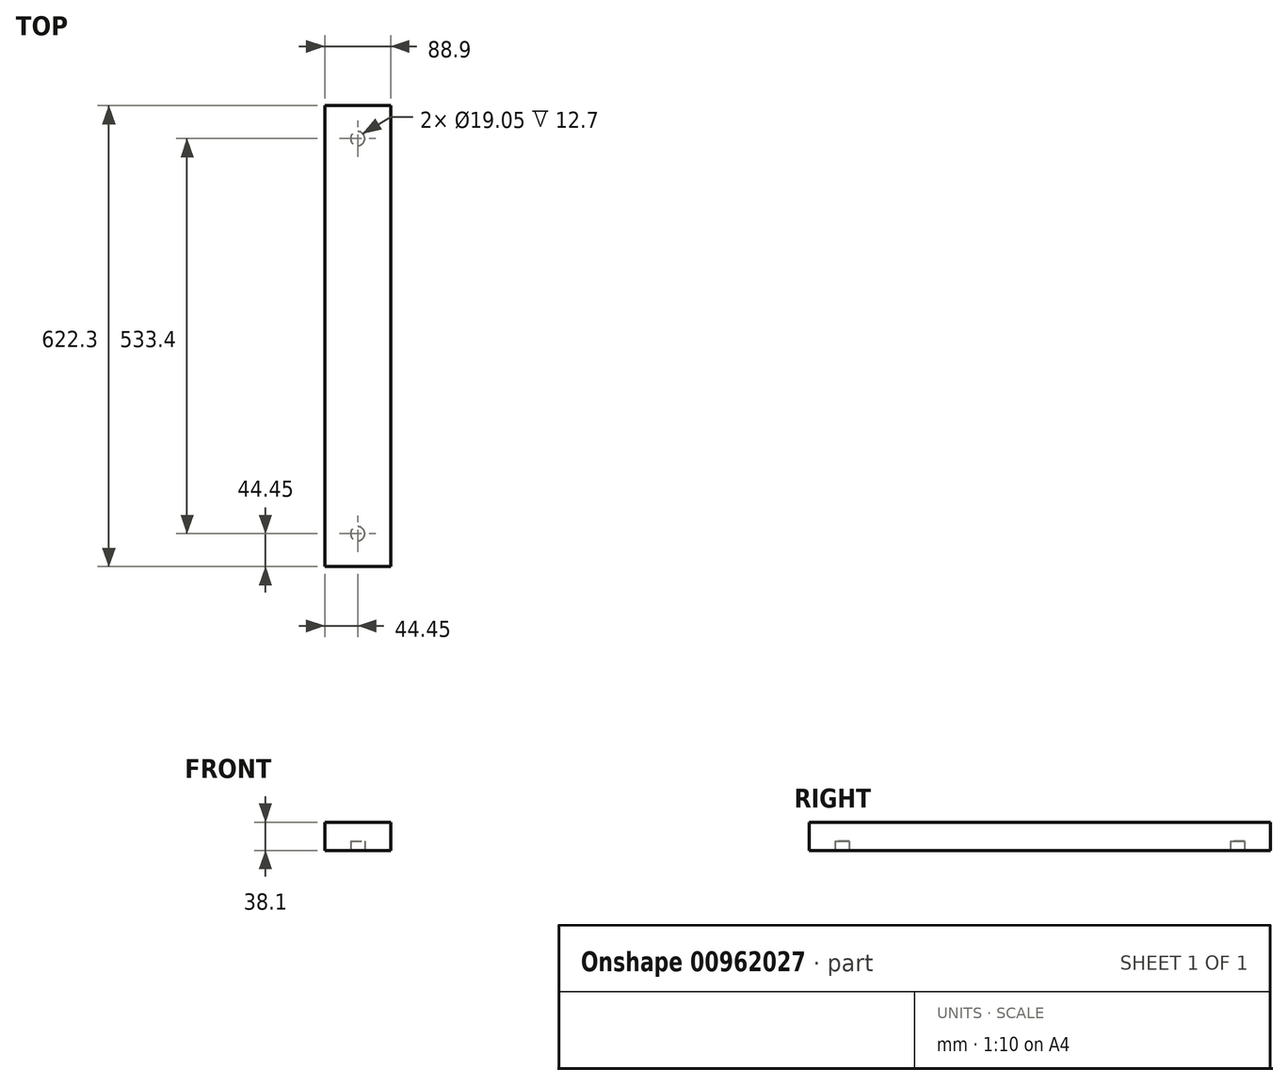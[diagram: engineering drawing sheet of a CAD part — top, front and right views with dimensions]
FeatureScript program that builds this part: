
annotation { "Feature Type Name" : "Feature", "Feature Type Description" : "" }
export const myFeature = defineFeature(function(context is Context, id is Id, definition is map)
    precondition{}
    {
        {
            var Q0;
            Q0=qCreatedBy(makeId("Front.planeOp"),FACE);
            var sketch = newSketch(context, id + "F0", { "sketchPlane" : qUnion([Q0])});
            skLineSegment(sketch, "E0.bottom", {"start": v(44.45, 19.05) * mm, "end": v(-44.45, 19.05) * mm});
            skLineSegment(sketch, "E0.top", {"start": v(44.45, -19.05) * mm, "end": v(-44.45, -19.05) * mm});
            skLineSegment(sketch, "E0.left", {"start": v(44.45, 19.05) * mm, "end": v(44.45, -19.05) * mm});
            skLineSegment(sketch, "E0.right", {"start": v(-44.45, 19.05) * mm, "end": v(-44.45, -19.05) * mm});
            skPoint(sketch, "E0.middle", {"position": v(0, 0) * mm});
            skSolve(sketch);
        }
        {
            var Q0;
            Q0 = qSketchRegion(id + "F0", true);
            extrude(context, id + "F1", {"entities" : qUnion([Q0]), "endBound" : BoundingType.SYMMETRIC, "depth" : 622.3 * mm, "offsetDistance" : 25.4 * mm});
        }
        {
            var Q0;
            Q0=makeQuery(id+"F1.opExtrude","SWEPT_FACE",FACE,{"disambiguationData":[OSD([sQuery(id+"F0.wireOp",EDGE,"E0.top")])]});
            var sketch = newSketch(context, id + "F2", { "sketchPlane" : qUnion([Q0])});
            skCircle(sketch, "E1", {"center": v(0, 266.7) * mm, "radius": 9.53 * mm});
            skCircle(sketch, "E2", {"center": v(0, -266.7) * mm, "radius": 9.53 * mm});
            skSolve(sketch);
        }
        {
            var Q0;
            Q0 = qSketchRegion(id + "F2", true);
            extrude(context, id + "F3", {"entities" : qUnion([Q0]), "operationType" : NewBodyOperationType.REMOVE, "oppositeDirection" : true, "depth" : 12.7 * mm, "offsetDistance" : 25.4 * mm});
        }
    });
